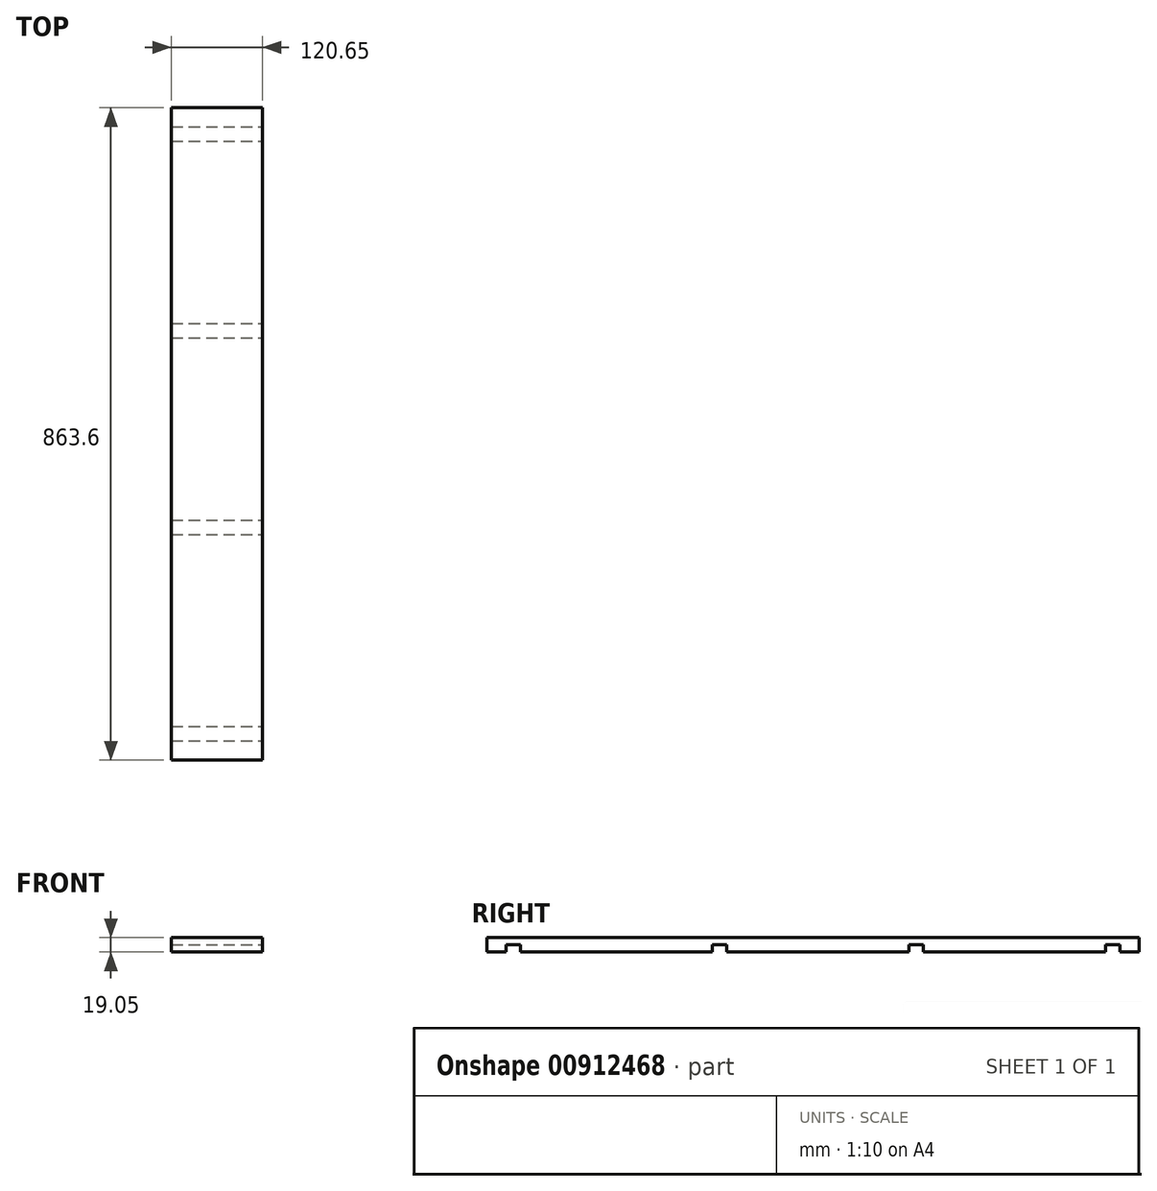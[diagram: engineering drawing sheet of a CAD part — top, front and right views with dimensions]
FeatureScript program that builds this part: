
annotation { "Feature Type Name" : "Feature", "Feature Type Description" : "" }
export const myFeature = defineFeature(function(context is Context, id is Id, definition is map)
    precondition{}
    {
        {
            var Q0;
            Q0=qCreatedBy(makeId("Front.planeOp"),FACE);
            var sketch = newSketch(context, id + "F0", { "sketchPlane" : qUnion([Q0])});
            skLineSegment(sketch, "E0.bottom", {"start": v(0, 0) * mm, "end": v(120.65, 0) * mm});
            skLineSegment(sketch, "E0.top", {"start": v(0, 19.05) * mm, "end": v(120.65, 19.05) * mm});
            skLineSegment(sketch, "E0.left", {"start": v(0, 0) * mm, "end": v(0, 19.05) * mm});
            skLineSegment(sketch, "E0.right", {"start": v(120.65, 0) * mm, "end": v(120.65, 19.05) * mm});
            skSolve(sketch);
        }
        {
            var Q0;
            Q0 = qSketchRegion(id + "F0", true);
            extrude(context, id + "F1", {"entities" : qUnion([Q0]), "depth" : 863.6 * mm, "offsetDistance" : 25.4 * mm});
        }
        {
            var Q0;
            Q0=makeQuery(id+"F1.opExtrude","SWEPT_FACE",FACE,{"disambiguationData":[OSD([sQuery(id+"F0.wireOp",EDGE,"E0.bottom")])]});
            var sketch = newSketch(context, id + "F2", { "sketchPlane" : qUnion([Q0])});
            skLineSegment(sketch, "E1.bottom", {"start": v(0, 838.2) * mm, "end": v(120.65, 838.2) * mm});
            skLineSegment(sketch, "E1.top", {"start": v(0, 819.15) * mm, "end": v(120.65, 819.15) * mm});
            skLineSegment(sketch, "E1.left", {"start": v(0, 838.2) * mm, "end": v(0, 819.15) * mm});
            skLineSegment(sketch, "E1.right", {"start": v(120.65, 838.2) * mm, "end": v(120.65, 819.15) * mm});
            skLineSegment(sketch, "E2.bottom", {"start": v(0, 25.4) * mm, "end": v(120.65, 25.4) * mm});
            skLineSegment(sketch, "E2.top", {"start": v(0, 44.45) * mm, "end": v(120.65, 44.45) * mm});
            skLineSegment(sketch, "E2.left", {"start": v(0, 25.4) * mm, "end": v(0, 44.45) * mm});
            skLineSegment(sketch, "E2.right", {"start": v(120.65, 25.4) * mm, "end": v(120.65, 44.45) * mm});
            skLineSegment(sketch, "E3.bottom", {"start": v(0, 285.75) * mm, "end": v(120.65, 285.75) * mm});
            skLineSegment(sketch, "E3.top", {"start": v(0, 304.8) * mm, "end": v(120.65, 304.8) * mm});
            skLineSegment(sketch, "E3.left", {"start": v(0, 285.75) * mm, "end": v(0, 304.8) * mm});
            skLineSegment(sketch, "E3.right", {"start": v(120.65, 285.75) * mm, "end": v(120.65, 304.8) * mm});
            skLineSegment(sketch, "E4.bottom", {"start": v(0, 565.15) * mm, "end": v(120.65, 565.15) * mm});
            skLineSegment(sketch, "E4.top", {"start": v(0, 546.1) * mm, "end": v(120.65, 546.1) * mm});
            skLineSegment(sketch, "E4.left", {"start": v(0, 565.15) * mm, "end": v(0, 546.1) * mm});
            skLineSegment(sketch, "E4.right", {"start": v(120.65, 565.15) * mm, "end": v(120.65, 546.1) * mm});
            skSolve(sketch);
        }
        {
            var Q0;
            Q0 = qSketchRegion(id + "F2", true);
            extrude(context, id + "F3", {"entities" : qUnion([Q0]), "operationType" : NewBodyOperationType.REMOVE, "oppositeDirection" : true, "depth" : 9.52 * mm, "offsetDistance" : 25.4 * mm});
        }
    });
